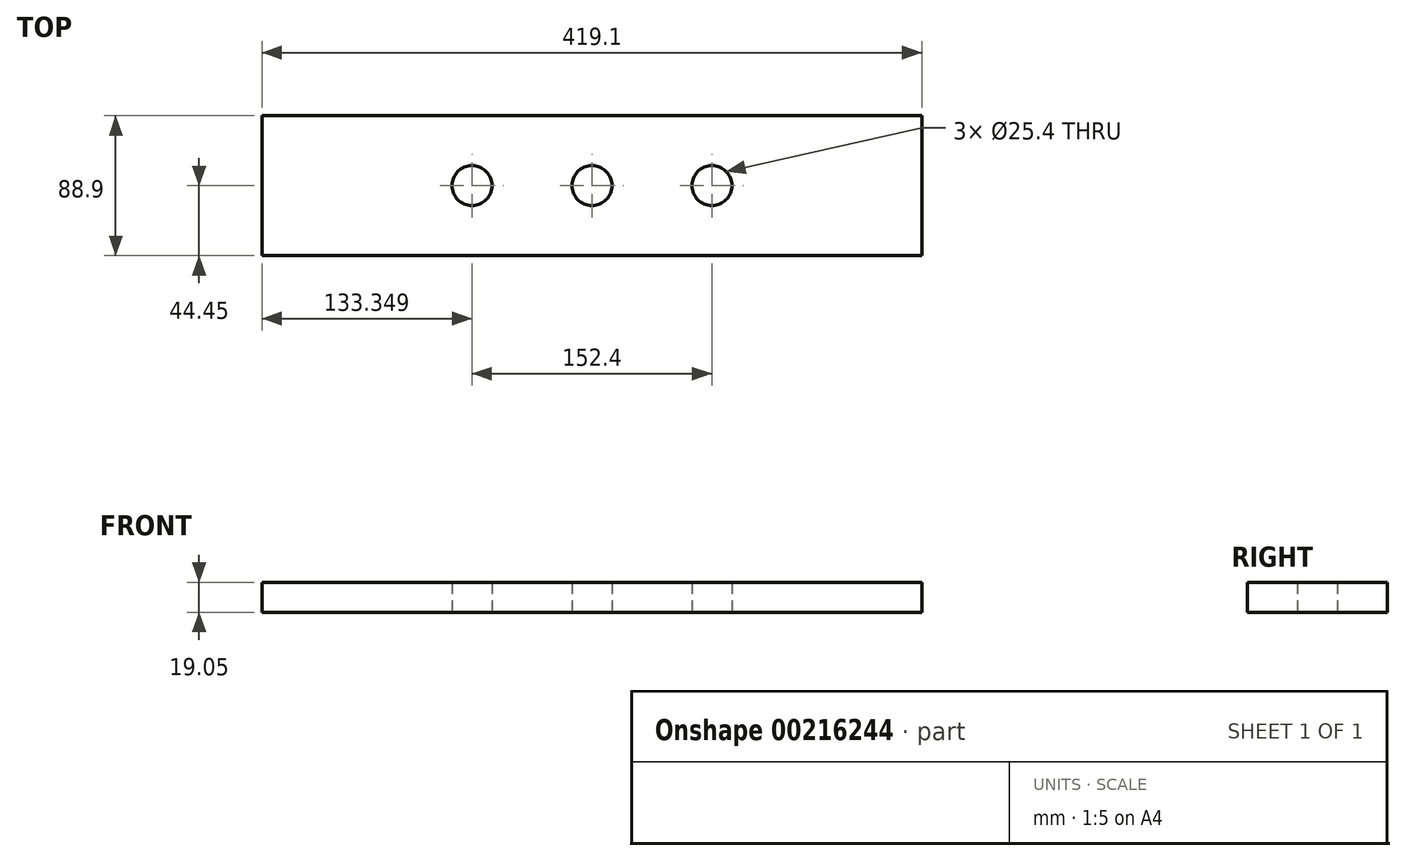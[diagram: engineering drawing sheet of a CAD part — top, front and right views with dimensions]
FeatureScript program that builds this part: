
annotation { "Feature Type Name" : "Feature", "Feature Type Description" : "" }
export const myFeature = defineFeature(function(context is Context, id is Id, definition is map)
    precondition{}
    {
        {
            var Q0;
            Q0=qCreatedBy(makeId("Top.planeOp"),FACE);
            var sketch = newSketch(context, id + "F0", { "sketchPlane" : qUnion([Q0])});
            skLineSegment(sketch, "E0", {"start": v(77.54, 105.41) * mm, "end": v(496.64, 105.41) * mm});
            skLineSegment(sketch, "E1", {"start": v(496.64, 105.41) * mm, "end": v(496.64, 194.31) * mm});
            skLineSegment(sketch, "E2", {"start": v(496.64, 194.31) * mm, "end": v(77.54, 194.31) * mm});
            skLineSegment(sketch, "E3", {"start": v(77.54, 194.31) * mm, "end": v(77.54, 105.41) * mm});
            skCircle(sketch, "E4", {"center": v(287.09, 149.86) * mm, "radius": 12.7 * mm});
            skCircle(sketch, "E5", {"center": v(363.29, 149.86) * mm, "radius": 12.7 * mm});
            skCircle(sketch, "E6", {"center": v(210.89, 149.86) * mm, "radius": 12.7 * mm});
            skSolve(sketch);
        }
        {
            var Q0;
            Q0=makeQuery(id+"F0.imprint","IMPRINT",FACE,{"disambiguationData":[TD([[makeQuery(id+"F0.imprint","IMPRINT",EDGE,{"derivedFrom":sQuery(id+"F0.wireOp",EDGE,"E0")}),1.0]])]});
            extrude(context, id + "F1", {"entities" : qUnion([Q0]), "depth" : 19.05 * mm});
        }
    });
